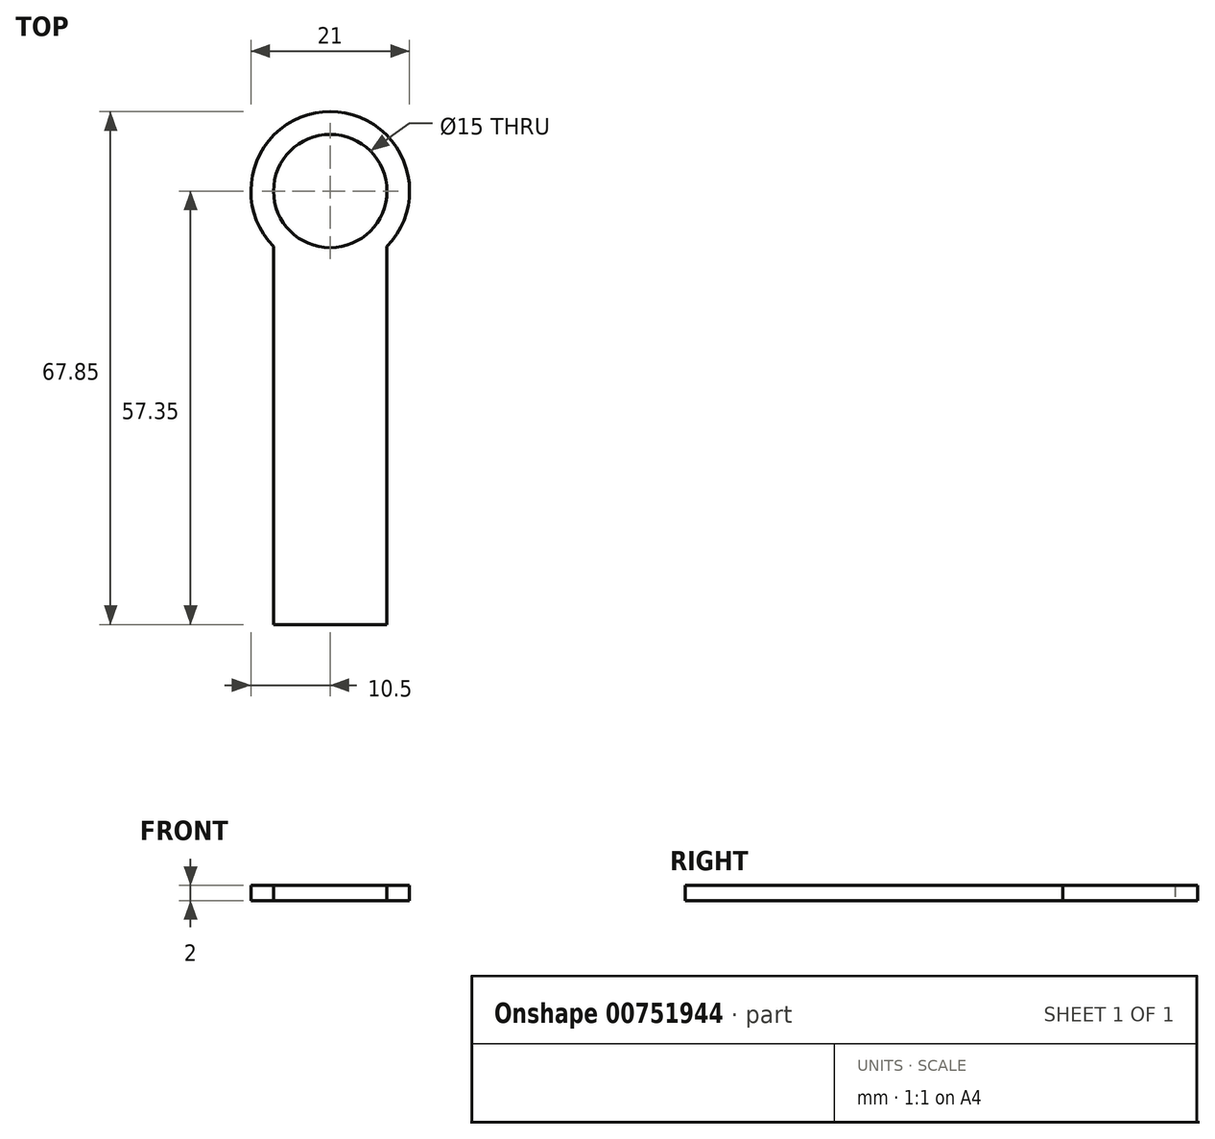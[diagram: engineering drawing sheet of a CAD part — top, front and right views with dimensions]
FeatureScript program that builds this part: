
annotation { "Feature Type Name" : "Feature", "Feature Type Description" : "" }
export const myFeature = defineFeature(function(context is Context, id is Id, definition is map)
    precondition{}
    {
        {
            var Q0;
            Q0=qCreatedBy(makeId("Top.planeOp"),FACE);
            var sketch = newSketch(context, id + "F0", { "sketchPlane" : qUnion([Q0])});
            skCircle(sketch, "E0", {"center": v(0, 0) * mm, "radius": 7.5 * mm});
            skArc(sketch, "E1.0", {"start": v(7.5, -7.35) * mm, "mid": v(0, 10.5) * mm, "end": v(-7.5, -7.35) * mm});
            skPoint(sketch, "E2", {"position": v(-7.5, 0) * mm});
            skPoint(sketch, "E3", {"position": v(7.5, 0) * mm});
            skLineSegment(sketch, "E4", {"start": v(-7.5, -7.35) * mm, "end": v(-7.5, -57.35) * mm});
            skLineSegment(sketch, "E5", {"start": v(7.5, -7.35) * mm, "end": v(7.5, -57.35) * mm});
            skLineSegment(sketch, "E6", {"start": v(-7.5, -57.35) * mm, "end": v(7.5, -57.35) * mm});
            skSolve(sketch);
        }
        {
            var Q0;
            Q0=makeQuery(id+"F0.imprint","IMPRINT",FACE,{"disambiguationData":[TD([[makeQuery(id+"F0.imprint","IMPRINT",EDGE,{"derivedFrom":sQuery(id+"F0.wireOp",EDGE,"E0")}),-1.0]])]});
            extrude(context, id + "F1", {"entities" : qUnion([Q0]), "depth" : 2 * mm, "offsetDistance" : 25.4 * mm});
        }
    });
